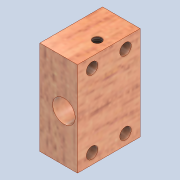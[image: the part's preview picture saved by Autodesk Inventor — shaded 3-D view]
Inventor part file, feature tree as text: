
AUTODESK INVENTOR PART (.ipt)
format: ipt  version: 2020 (Build 240168000, 168)  size: 228,864 bytes
history: native  units: mm
features: sketch x4, extrude x3, pattern_linear x1, hole x1
ambient origin geometry x8: Origin, YZ Plane, XZ Plane, XY Plane, X Axis, Y Axis, Z Axis, Center Point
bodies: Solid1 (feature_tree)
feature tree (9):
  extrude  "Extrusion1"  Depth=45.0mm
  extrude  "Extrusion2"  Depth=10.8mm
  extrude  "Extrusion3"  TaperAngle=0.0deg  [1 undecoded]
  pattern_linear  "Rectangular Pattern1"  Spacing1=5.5mm  [1 undecoded]
  hole  "Hole1"  [1 undecoded]
  sketch  "Sketch1"  dims[d0=18.0mm d1=45.0mm]
  sketch  "Sketch3"  dims[d2=30.0mm d3=0.0mm d4=10.8mm]
  sketch  "Sketch4"  dims[d5=6.5mm d6=0.0mm d7=0.0mm]
  sketch  "Sketch5"  dims[d8=5.5mm d9=5.5mm d10=7.0mm d11=5.0mm d12=5.0mm d13=7.0mm d14=0.0mm d15=0.0mm d16=35.0mm d17=16.0mm d18=20.0mm d20=16.0mm d21=20.0mm d23=35.0mm d24=4.134mm d25=45.0mm d26=4.0mm d27=2.0mm d28=90.0deg d29=8.0mm d30=20.594885mm d38=12.5mm]
note: 3 required parameter values undecoded (feature->parameter linkage not recoverable at this tier; creation-order binding heuristic only, values carry confidence <= 0.55)
